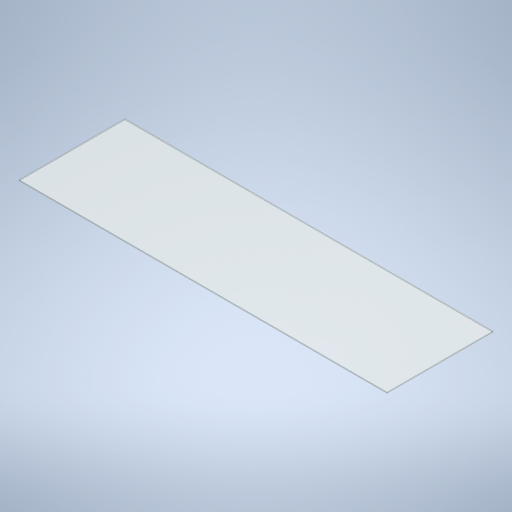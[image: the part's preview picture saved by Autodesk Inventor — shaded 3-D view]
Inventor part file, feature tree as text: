
AUTODESK INVENTOR PART (.ipt)
format: ipt  version: 2024 (Build 280153000, 153)  size: 231,424 bytes
history: native  units: in
note: dims shown in document units (in); Inventor stores cm internally (conversion verified against a paired STEP export)
features: extrude x1, sketch x1
ambient origin geometry x8: Origin, YZ Plane, XZ Plane, XY Plane, X Axis, Y Axis, Z Axis, Center Point
bodies: Solid1 (feature_tree)
feature tree (2):
  extrude  "Extrusion1"  Depth=291.5in
  sketch  "Sketch1"  dims[d2=83.792in d3=291.5in d4=0.75in d5=0.0in]
